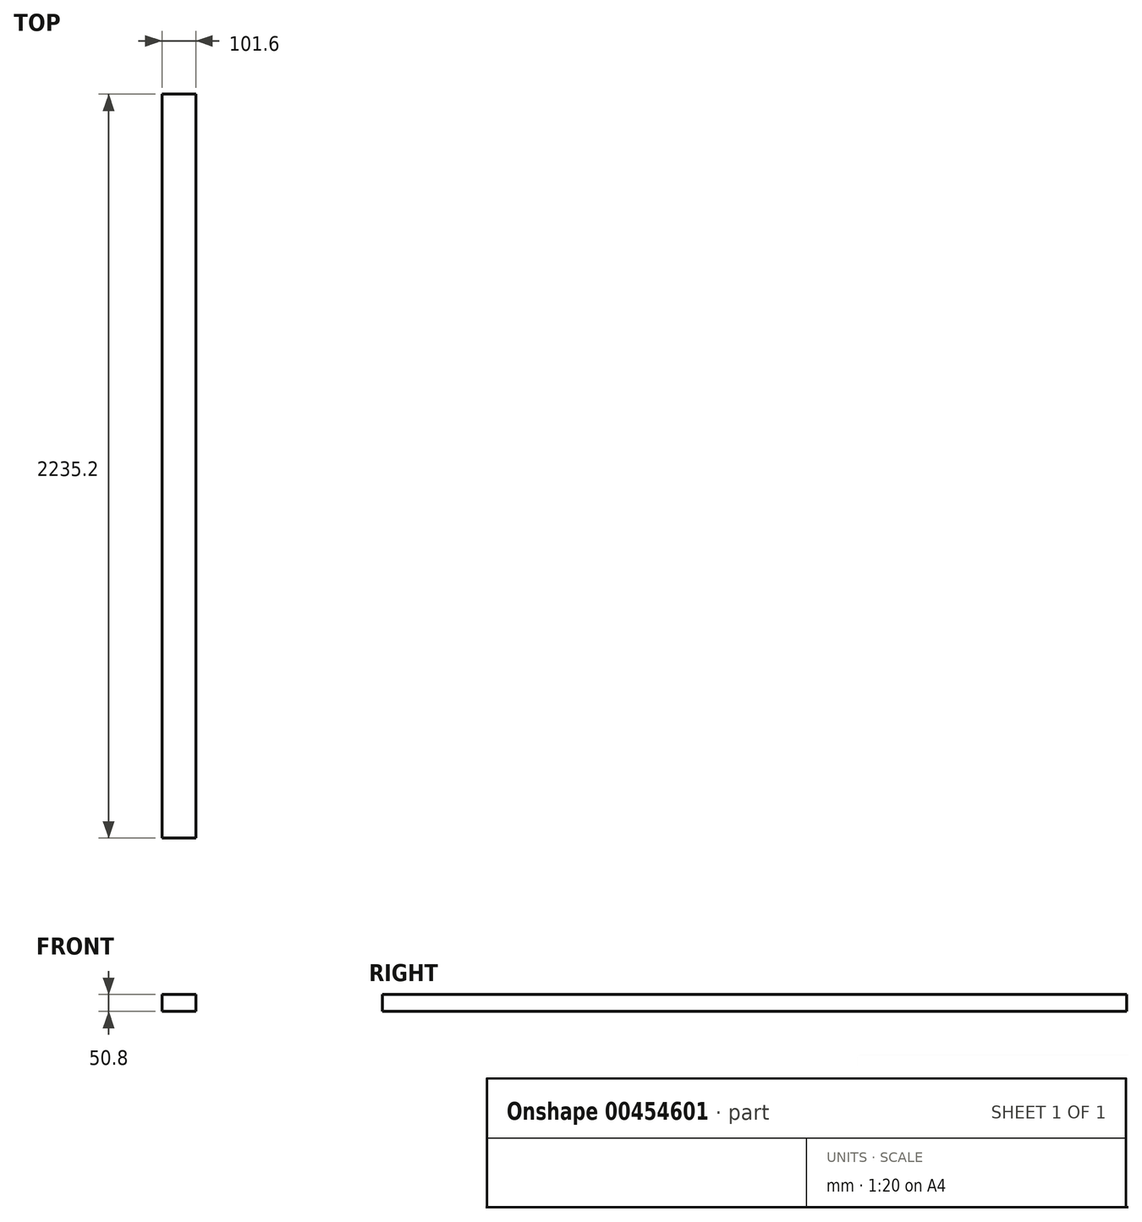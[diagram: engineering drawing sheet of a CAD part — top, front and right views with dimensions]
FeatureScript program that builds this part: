
annotation { "Feature Type Name" : "Feature", "Feature Type Description" : "" }
export const myFeature = defineFeature(function(context is Context, id is Id, definition is map)
    precondition{}
    {
        {
            var Q0;
            Q0=qCreatedBy(makeId("Front.planeOp"),FACE);
            var sketch = newSketch(context, id + "F0", { "sketchPlane" : qUnion([Q0])});
            skLineSegment(sketch, "E0.bottom", {"start": v(50.8, 25.4) * mm, "end": v(-50.8, 25.4) * mm});
            skLineSegment(sketch, "E0.top", {"start": v(50.8, -25.4) * mm, "end": v(-50.8, -25.4) * mm});
            skLineSegment(sketch, "E0.left", {"start": v(50.8, 25.4) * mm, "end": v(50.8, -25.4) * mm});
            skLineSegment(sketch, "E0.right", {"start": v(-50.8, 25.4) * mm, "end": v(-50.8, -25.4) * mm});
            skPoint(sketch, "E0.middle", {"position": v(0, 0) * mm});
            skSolve(sketch);
        }
        {
            var Q0;
            Q0=makeQuery(id+"F0.imprint","IMPRINT",FACE,{"disambiguationData":[TD([[makeQuery(id+"F0.imprint","IMPRINT",EDGE,{"derivedFrom":sQuery(id+"F0.wireOp",EDGE,"E0.bottom")}),1.0]])]});
            extrude(context, id + "F1", {"entities" : qUnion([Q0]), "depth" : 2235.2 * mm});
        }
    });
